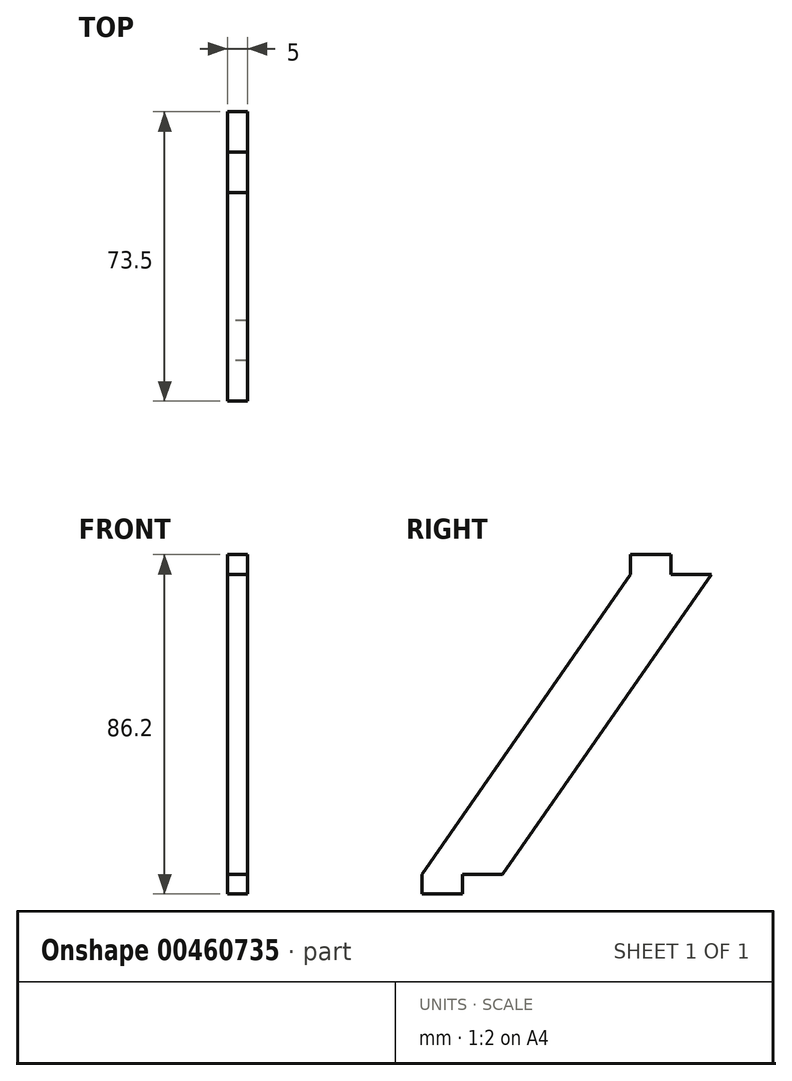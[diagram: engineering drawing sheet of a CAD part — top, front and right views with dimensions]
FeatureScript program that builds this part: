
annotation { "Feature Type Name" : "Feature", "Feature Type Description" : "" }
export const myFeature = defineFeature(function(context is Context, id is Id, definition is map)
    precondition{}
    {
        {
            var Q0;
            Q0=qCreatedBy(makeId("Right.planeOp"),FACE);
            var sketch = newSketch(context, id + "F0", { "sketchPlane" : qUnion([Q0])});
            skLineSegment(sketch, "E0", {"start": v(0, 0) * mm, "end": v(-53, -76.2) * mm});
            skLineSegment(sketch, "E1", {"start": v(-53, -76.2) * mm, "end": v(-63.25, -76.2) * mm});
            skLineSegment(sketch, "E2", {"start": v(-63.25, -76.2) * mm, "end": v(-63.25, -81.2) * mm});
            skLineSegment(sketch, "E3", {"start": v(-63.25, -81.2) * mm, "end": v(-73.5, -81.2) * mm});
            skLineSegment(sketch, "E4", {"start": v(-73.5, -81.2) * mm, "end": v(-73.5, -76.2) * mm});
            skLineSegment(sketch, "E5", {"start": v(-73.5, -76.2) * mm, "end": v(-20.5, 0) * mm});
            skLineSegment(sketch, "E6", {"start": v(-20.5, 0) * mm, "end": v(-20.5, 5) * mm});
            skLineSegment(sketch, "E7", {"start": v(-20.5, 5) * mm, "end": v(-10.25, 5) * mm});
            skLineSegment(sketch, "E8", {"start": v(-10.25, 5) * mm, "end": v(-10.25, 0) * mm});
            skLineSegment(sketch, "E9", {"start": v(-10.25, 0) * mm, "end": v(0, 0) * mm});
            skPoint(sketch, "E10", {"position": v(-53, -76.2) * mm});
            skPoint(sketch, "E11", {"position": v(0, -76.2) * mm});
            skPoint(sketch, "E12", {"position": v(0, 5) * mm});
            skPoint(sketch, "E13", {"position": v(0, -81.2) * mm});
            skPoint(sketch, "E14", {"position": v(-73.5, 5) * mm});
            skPoint(sketch, "E15", {"position": v(14.5, 0) * mm});
            skPoint(sketch, "E16", {"position": v(14.5, -76.27) * mm});
            skSolve(sketch);
        }
        {
            var Q0;
            Q0=makeQuery(id+"F0.imprint","IMPRINT",FACE,{"disambiguationData":[TD([[makeQuery(id+"F0.imprint","IMPRINT",EDGE,{"derivedFrom":sQuery(id+"F0.wireOp",EDGE,"E0")}),-1.0]])]});
            extrude(context, id + "F1", {"entities" : qUnion([Q0]), "depth" : 5 * mm});
        }
    });
